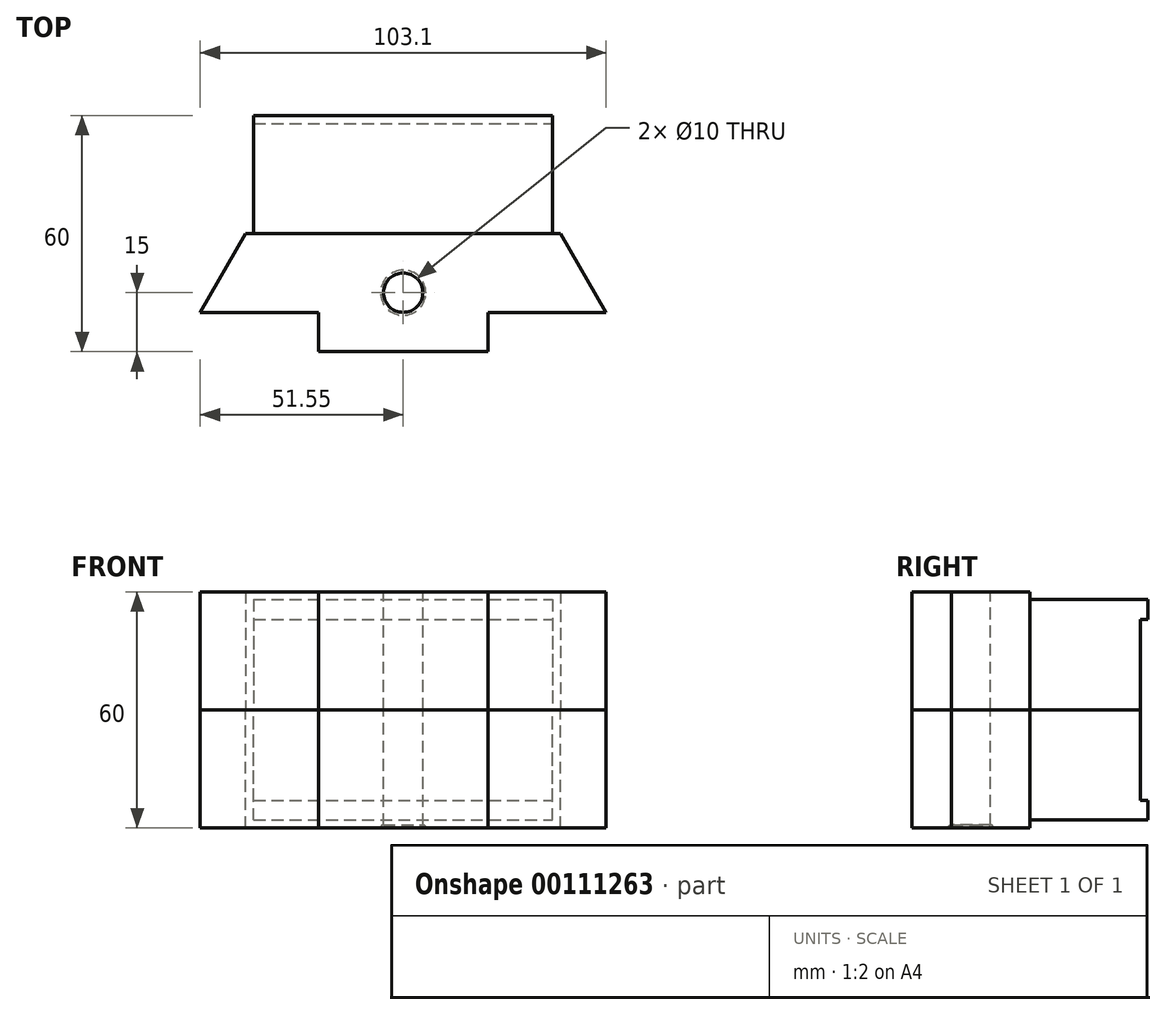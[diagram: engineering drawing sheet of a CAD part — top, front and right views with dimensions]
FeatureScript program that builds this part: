
annotation { "Feature Type Name" : "Feature", "Feature Type Description" : "" }
export const myFeature = defineFeature(function(context is Context, id is Id, definition is map)
    precondition{}
    {
        {
            var Q0;
            Q0=qCreatedBy(makeId("Top.planeOp"),FACE);
            var sketch = newSketch(context, id + "F0", { "sketchPlane" : qUnion([Q0])});
            skLineSegment(sketch, "E0", {"start": v(0, 53.64) * mm, "end": v(0, -60) * mm, "construction": true});
            skLineSegment(sketch, "E1", {"start": v(-40, 0) * mm, "end": v(-51.55, -20) * mm});
            skLineSegment(sketch, "E2", {"start": v(-51.55, -20) * mm, "end": v(-21.55, -20) * mm});
            skLineSegment(sketch, "E3", {"start": v(-21.55, -20) * mm, "end": v(-21.55, -30) * mm});
            skLineSegment(sketch, "E4.MirrorCS", {"start": v(21.55, -20) * mm, "end": v(21.55, -30) * mm});
            skLineSegment(sketch, "E5.MirrorCS", {"start": v(51.55, -20) * mm, "end": v(21.55, -20) * mm});
            skLineSegment(sketch, "E6.MirrorCS", {"start": v(40, 0) * mm, "end": v(51.55, -20) * mm});
            skLineSegment(sketch, "E7", {"start": v(-40, 0) * mm, "end": v(40, 0) * mm});
            skLineSegment(sketch, "E8", {"start": v(-21.55, -30) * mm, "end": v(21.55, -30) * mm});
            skSolve(sketch);
        }
        {
            var Q0;
            Q0=makeQuery(id+"F0.imprint","IMPRINT",FACE,{"disambiguationData":[TD([[makeQuery(id+"F0.imprint","IMPRINT",EDGE,{"derivedFrom":sQuery(id+"F0.wireOp",EDGE,"E1")}),1.0]])]});
            extrude(context, id + "F1", {"entities" : qUnion([Q0]), "depth" : 30 * mm});
        }
        {
            var Q0;
            Q0=makeQuery(id+"F1.opExtrude","SWEPT_FACE",FACE,{"disambiguationData":[OSD([sQuery(id+"F0.wireOp",EDGE,"E7")])]});
            var sketch = newSketch(context, id + "F2", { "sketchPlane" : qUnion([Q0])});
            skLineSegment(sketch, "E9.0", {"start": v(40, 0) * mm, "end": v(-40, 0) * mm, "construction": true});
            skLineSegment(sketch, "E9.1", {"start": v(-40, 30) * mm, "end": v(-40, 0) * mm, "construction": true});
            skLineSegment(sketch, "E9.2", {"start": v(40, 30) * mm, "end": v(-40, 30) * mm, "construction": true});
            skLineSegment(sketch, "E9.3", {"start": v(40, 30) * mm, "end": v(40, 0) * mm, "construction": true});
            skLineSegment(sketch, "E10.1", {"start": v(38, 28) * mm, "end": v(38, 0) * mm});
            skLineSegment(sketch, "E10.2", {"start": v(38, 28) * mm, "end": v(-38, 28) * mm});
            skLineSegment(sketch, "E10.3", {"start": v(-38, 28) * mm, "end": v(-38, 0) * mm});
            skLineSegment(sketch, "E11", {"start": v(38, 0) * mm, "end": v(-38, 0) * mm});
            skSolve(sketch);
        }
        {
            var Q0;
            Q0 = qSketchRegion(id + "F2", true);
            var Q1;
            Q1=makeQuery(id+"F2.imprint","IMPRINT",FACE,{"disambiguationData":[TD([[makeQuery(id+"F2.imprint","IMPRINT",EDGE,{"derivedFrom":sQuery(id+"F2.wireOp",EDGE,"E10.0")}),-1.0]])]});
            extrude(context, id + "F3", {"entities" : qUnion([Q0, Q1]), "operationType" : NewBodyOperationType.ADD, "depth" : 30 * mm});
        }
        {
            var Q0;
            Q0=makeQuery(id+"F3.opExtrude","CAP_FACE",FACE,{"disambiguationData":[OSD([sQuery(id+"F2.wireOp",EDGE,"E10.1"),sQuery(id+"F2.wireOp",EDGE,"E10.2"),sQuery(id+"F2.wireOp",EDGE,"E10.3"),sQuery(id+"F2.wireOp",EDGE,"E11")])],"isStart":false});
            var sketch = newSketch(context, id + "F4", { "sketchPlane" : qUnion([Q0])});
            skLineSegment(sketch, "E12", {"start": v(38, 0) * mm, "end": v(38, 23) * mm});
            skLineSegment(sketch, "E13", {"start": v(38, 23) * mm, "end": v(-38, 23) * mm});
            skLineSegment(sketch, "E14", {"start": v(-38, 23) * mm, "end": v(-38, 0) * mm});
            skLineSegment(sketch, "E15", {"start": v(-38, 0) * mm, "end": v(38, 0) * mm});
            skSolve(sketch);
        }
        {
            var Q0;
            Q0 = qSketchRegion(id + "F4", true);
            extrude(context, id + "F5", {"entities" : qUnion([Q0]), "operationType" : NewBodyOperationType.REMOVE, "oppositeDirection" : true, "depth" : 2 * mm});
        }
        {
            var Q0;
            Q0=makeQuery(id+"F1.opExtrude","SWEPT_BODY",BODY,{"disambiguationData":[OSD([sQuery(id+"F0.wireOp",EDGE,"E1"),sQuery(id+"F0.wireOp",EDGE,"E2"),sQuery(id+"F0.wireOp",EDGE,"E3"),sQuery(id+"F0.wireOp",EDGE,"E4.MirrorCS"),sQuery(id+"F0.wireOp",EDGE,"E5.MirrorCS"),sQuery(id+"F0.wireOp",EDGE,"E6.MirrorCS"),sQuery(id+"F0.wireOp",EDGE,"E7"),sQuery(id+"F0.wireOp",EDGE,"E8")])]});
            var Q1;
            Q1=qCreatedBy(makeId("Top.planeOp"),FACE);
            mirror(context, id + "F6", {"entities" : qUnion([Q0]), "mirrorPlane" : qUnion([Q1])});
        }
        {
            var Q0;
            Q0=makeQuery(id+"F1.opExtrude","CAP_FACE",FACE,{"disambiguationData":[OSD([sQuery(id+"F0.wireOp",EDGE,"E1"),sQuery(id+"F0.wireOp",EDGE,"E2"),sQuery(id+"F0.wireOp",EDGE,"E3"),sQuery(id+"F0.wireOp",EDGE,"E4.MirrorCS"),sQuery(id+"F0.wireOp",EDGE,"E5.MirrorCS"),sQuery(id+"F0.wireOp",EDGE,"E6.MirrorCS"),sQuery(id+"F0.wireOp",EDGE,"E7"),sQuery(id+"F0.wireOp",EDGE,"E8")])],"isStart":false});
            var sketch = newSketch(context, id + "F7", { "sketchPlane" : qUnion([Q0])});
            skLineSegment(sketch, "E16", {"start": v(0, -30) * mm, "end": v(0, 0) * mm, "construction": true});
            skCircle(sketch, "E17", {"center": v(0, -15) * mm, "radius": 5 * mm});
            skSolve(sketch);
        }
        {
            var Q0;
            Q0=makeQuery(id+"F7.imprint","IMPRINT",FACE,{"disambiguationData":[TD([[makeQuery(id+"F7.imprint","IMPRINT",EDGE,{"derivedFrom":sQuery(id+"F7.wireOp",EDGE,"E17")}),1.0]])]});
            var Q1;
            Q1=makeQuery(id+"F6.opPattern","COPY",FACE,{"derivedFrom":makeQuery(id+"F1.opExtrude","CAP_FACE",FACE,{"disambiguationData":[OSD([sQuery(id+"F0.wireOp",EDGE,"E1"),sQuery(id+"F0.wireOp",EDGE,"E2"),sQuery(id+"F0.wireOp",EDGE,"E3"),sQuery(id+"F0.wireOp",EDGE,"E4.MirrorCS"),sQuery(id+"F0.wireOp",EDGE,"E5.MirrorCS"),sQuery(id+"F0.wireOp",EDGE,"E6.MirrorCS"),sQuery(id+"F0.wireOp",EDGE,"E7"),sQuery(id+"F0.wireOp",EDGE,"E8")])],"isStart":false}),"instanceName":"1"});
            extrude(context, id + "F8", {"entities" : qUnion([Q0]), "operationType" : NewBodyOperationType.REMOVE, "endBound" : BoundingType.UP_TO_SURFACE, "oppositeDirection" : true, "endBoundEntityFace" : qUnion([Q1]), "depth" : 45 * mm});
        }
        {
            var Q0;
            Q0=qCreatedBy(makeId("Right.planeOp"),FACE);
            var sketch = newSketch(context, id + "F9", { "sketchPlane" : qUnion([Q0])});
            skLineSegment(sketch, "E18.0", {"start": v(-20, -30) * mm, "end": v(-10, -30) * mm, "construction": true});
            skCircle(sketch, "E19", {"center": v(-10, -30) * mm, "radius": 0.75 * mm});
            skLineSegment(sketch, "E20", {"start": v(-15, -30) * mm, "end": v(-15, -35) * mm, "construction": true});
            skSolve(sketch);
        }
        {
            var Q0;
            Q0=makeQuery(id+"F9.imprint","IMPRINT",FACE,{"disambiguationData":[TD([[makeQuery(id+"F9.imprint","IMPRINT",EDGE,{"derivedFrom":sQuery(id+"F9.wireOp",EDGE,"E19")}),1.0]])]});
            var Q1;
            Q1=sQuery(id+"F9.wireOp",EDGE,"E20");
            revolve(context, id + "F10", {"operationType" : NewBodyOperationType.REMOVE, "entities" : qUnion([Q0]), "axis" : qUnion([Q1]), "revolveType" : RevolveType.FULL, "oppositeDirection" : true});
        }
    });
